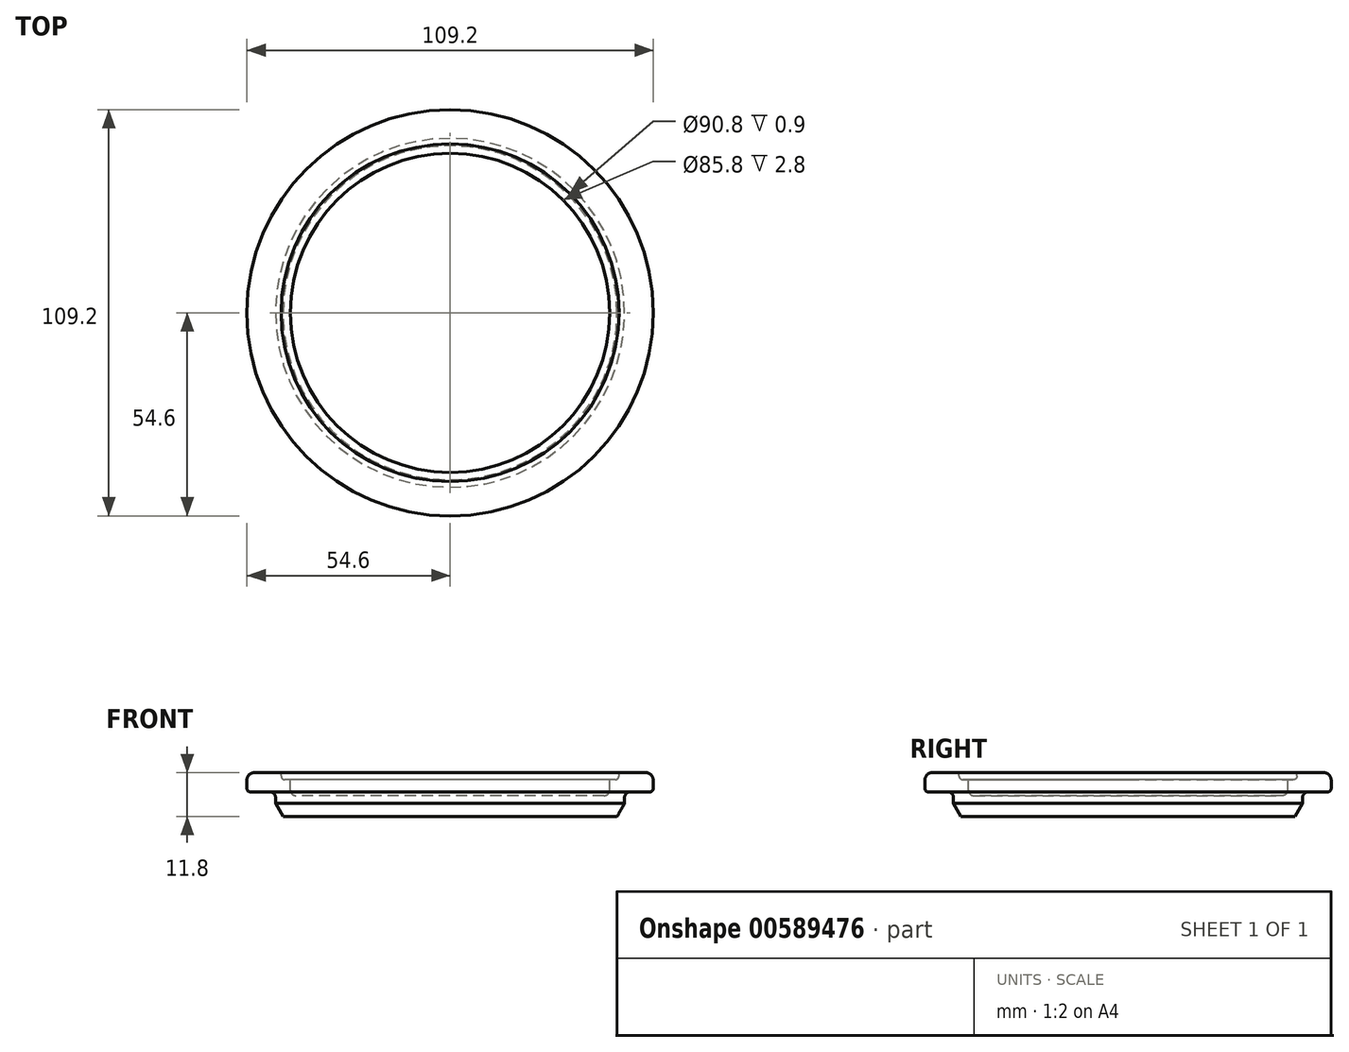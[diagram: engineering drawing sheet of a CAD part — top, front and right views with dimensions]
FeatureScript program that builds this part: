
annotation { "Feature Type Name" : "Feature", "Feature Type Description" : "" }
export const myFeature = defineFeature(function(context is Context, id is Id, definition is map)
    precondition{}
    {
        {
            var Q0;
            Q0=qCreatedBy(makeId("Front.planeOp"),FACE);
            var sketch = newSketch(context, id + "F0", { "sketchPlane" : qUnion([Q0])});
            skLineSegment(sketch, "E0", {"start": v(54.6, 9.8) * mm, "end": v(54.6, 7.6) * mm});
            skLineSegment(sketch, "E1", {"start": v(53.6, 6.6) * mm, "end": v(48.4, 6.6) * mm});
            skLineSegment(sketch, "E2", {"start": v(46.9, 5.1) * mm, "end": v(46.9, 3.5) * mm});
            skLineSegment(sketch, "E3", {"start": v(46.9, 3.5) * mm, "end": v(44.88, 0) * mm});
            skLineSegment(sketch, "E4", {"start": v(44.88, 0) * mm, "end": v(0, 0) * mm});
            skPoint(sketch, "E5.visualSharp", {"position": v(46.9, 6.6) * mm});
            skArc(sketch, "E5.filletArc", {"start": v(48.4, 6.6) * mm, "mid": v(47.34, 6.16) * mm, "end": v(46.9, 5.1) * mm});
            skLineSegment(sketch, "E6", {"start": v(0, 5.6) * mm, "end": v(41.4, 5.6) * mm});
            skLineSegment(sketch, "E7", {"start": v(42.9, 7.1) * mm, "end": v(42.9, 9.9) * mm});
            skLineSegment(sketch, "E8", {"start": v(42.9, 9.9) * mm, "end": v(44.4, 9.9) * mm});
            skLineSegment(sketch, "E9", {"start": v(45.4, 10.9) * mm, "end": v(45.4, 11.8) * mm});
            skLineSegment(sketch, "E10", {"start": v(45.4, 11.8) * mm, "end": v(52.6, 11.8) * mm});
            skLineSegment(sketch, "E11", {"start": v(0, 5.6) * mm, "end": v(0, 0) * mm});
            skPoint(sketch, "E12.visualSharp", {"position": v(42.9, 5.6) * mm});
            skArc(sketch, "E12.filletArc", {"start": v(41.4, 5.6) * mm, "mid": v(42.46, 6.04) * mm, "end": v(42.9, 7.1) * mm});
            skPoint(sketch, "E13.visualSharp", {"position": v(45.4, 9.9) * mm});
            skArc(sketch, "E13.filletArc", {"start": v(44.4, 9.9) * mm, "mid": v(45.1, 10.2) * mm, "end": v(45.4, 10.9) * mm});
            skPoint(sketch, "E14.visualSharp", {"position": v(54.6, 11.8) * mm});
            skArc(sketch, "E14.filletArc", {"start": v(54.6, 9.8) * mm, "mid": v(54.01, 11.21) * mm, "end": v(52.6, 11.8) * mm});
            skPoint(sketch, "E15.visualSharp", {"position": v(54.6, 6.6) * mm});
            skArc(sketch, "E15.filletArc", {"start": v(53.6, 6.6) * mm, "mid": v(54.3, 6.9) * mm, "end": v(54.6, 7.6) * mm});
            skSolve(sketch);
        }
        {
            var Q0;
            Q0 = qSketchRegion(id + "F0", true);
            var Q1;
            Q1=sQuery(id+"F0.wireOp",EDGE,"E11");
            revolve(context, id + "F1", {"entities" : qUnion([Q0]), "axis" : qUnion([Q1]), "revolveType" : RevolveType.FULL});
        }
    });
